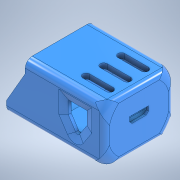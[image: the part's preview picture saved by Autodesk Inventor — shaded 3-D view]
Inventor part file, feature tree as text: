
AUTODESK INVENTOR PART (.ipt)
format: ipt  version: 2020 (Build 240168000, 168)  size: 587,264 bytes
history: native  units: in
note: dims shown in document units (in); Inventor stores cm internally (conversion verified against a paired STEP export)
features: extrude x13, sketch x7, chamfer x6, fillet x5, other x3, revolve x2, projected_geometry x2, mirror x1, plane x1, boolean_combine x1
ambient origin geometry x8: Origin, YZ Plane, XZ Plane, XY Plane, X Axis, Y Axis, Z Axis, Center Point
bodies: Solid4 (feature_tree), Solid2 (feature_tree)
feature tree (41):
  other  "SmartEgg Housing Main.ipt"
  extrude  "Extrusion1"  Depth=0.3937in
  extrude  "Extrusion2"  Depth=0.0492in TaperAngle=0.0deg
  extrude  "Extrusion3"  Depth=0.0394in
  fillet  "Fillet1"  Radius=0.0787in
  fillet  "Fillet2"  Radius=0.1181in
  fillet  "Fillet3"  Radius=0.0787in
  fillet  "Fillet4"  Radius=0.5659in
  sketch  "Sketch5"  dims[d5=0.0394in d6=0.0in d7=0.0394in d8=0.0787in d9=0.1181in d10=0.0787in d11=0.5659in d12=0.0in]
  extrude  "Extrusion6"  TaperAngle=0.0deg  [1 undecoded]
  extrude  "Extrusion7"  Depth=0.0394in
  extrude  "Extrusion8"  TaperAngle=45.0deg  [1 undecoded]
  chamfer  "Chamfer2"  Distance=0.0394in
  fillet  "Fillet5"  Radius=0.0394in
  extrude  "Extrusion13"  Depth=0.0591in
  mirror  "Mirror1"
  extrude  "Extrusion4"  Depth=0.1181in
  extrude  "Extrusion5"  Depth=0.3937in TaperAngle=0.0deg
  chamfer  "Chamfer1"  Distance=0.0354in
  extrude  "Extrusion9"  TaperAngle=0.0deg  [1 undecoded]
  chamfer  "Chamfer7"  Distance=0.1476in
  chamfer  "Chamfer8"  Distance=0.0591in
  chamfer  "Chamfer9"  Angle=45.0deg  [1 undecoded]
  chamfer  "Chamfer10"  Distance=0.0591in
  sketch  "Sketch7"  dims[d16=0.0394in d17=0.0787in d18=45.0deg d19=0.4528in]
  sketch  "Sketch8"  dims[d20=0.0787in d23=45.0deg]
  plane  "Work Plane2"
  other  "Housing Largest Area"
  revolve  "Revolution1"  [1 undecoded]
  revolve  "Revolution2"  [1 undecoded]
  extrude  "Extrusion10"  Depth=0.1181in TaperAngle=0.0deg
  boolean_combine  "Combine1"
  sketch  "Sketch10"  dims[d24=45.0deg d25=0.0394in d26=0.0394in d31=0.0591in d32=0.1969in d33=0.3937in d34=0.0in d35=0.0354in d36=0.0in d37=0.1476in d38=0.0in d39=0.0591in d40=0.0354in d41=45.0deg d42=0.0591in d43=0.0394in d58=0.1181in d59=0.5659in d60=0.0in d62=0.0394in d63=0.1181in d64=0.0394in d65=75.0deg d66=0.1181in d67=0.0394in d68=75.0deg d69=0.1181in d70=0.0394in d71=75.0deg d72=0.1181in d73=0.0394in d74=75.0deg d75=90.0deg d76=0.1772in d77=90.0deg d78=0.1378in d79=360.0deg d80=0.9744in d81=0.0in d83=0.0591in d84=0.0591in d85=0.0591in d86=0.5906in d87=0.3937in d88=0.3937in d89=0.1181in d90=0.0in d91=0.1181in d92=0.0in d93=0.0787in d94=0.0in d95=0.1181in]
  extrude  "Extrusion11"  Depth=0.0394in
  extrude  "Extrusion12"  Depth=0.1181in TaperAngle=75.0deg
  sketch  "Sketch3"  dims[d0=0.3937in d1=0.4872in]
  other  "ESP32 Feather"
  sketch  "Sketch4"  dims[d2=0.0in d3=0.0492in d4=0.0in]
  sketch  "Sketch6"  dims[d13=0.315in d14=0.0in d15=0.0in]
  projected_geometry  "Project Cut Edges1"
  projected_geometry  "Project Cut Edges2"
note: 6 required parameter values undecoded (feature->parameter linkage not recoverable at this tier; creation-order binding heuristic only, values carry confidence <= 0.55)